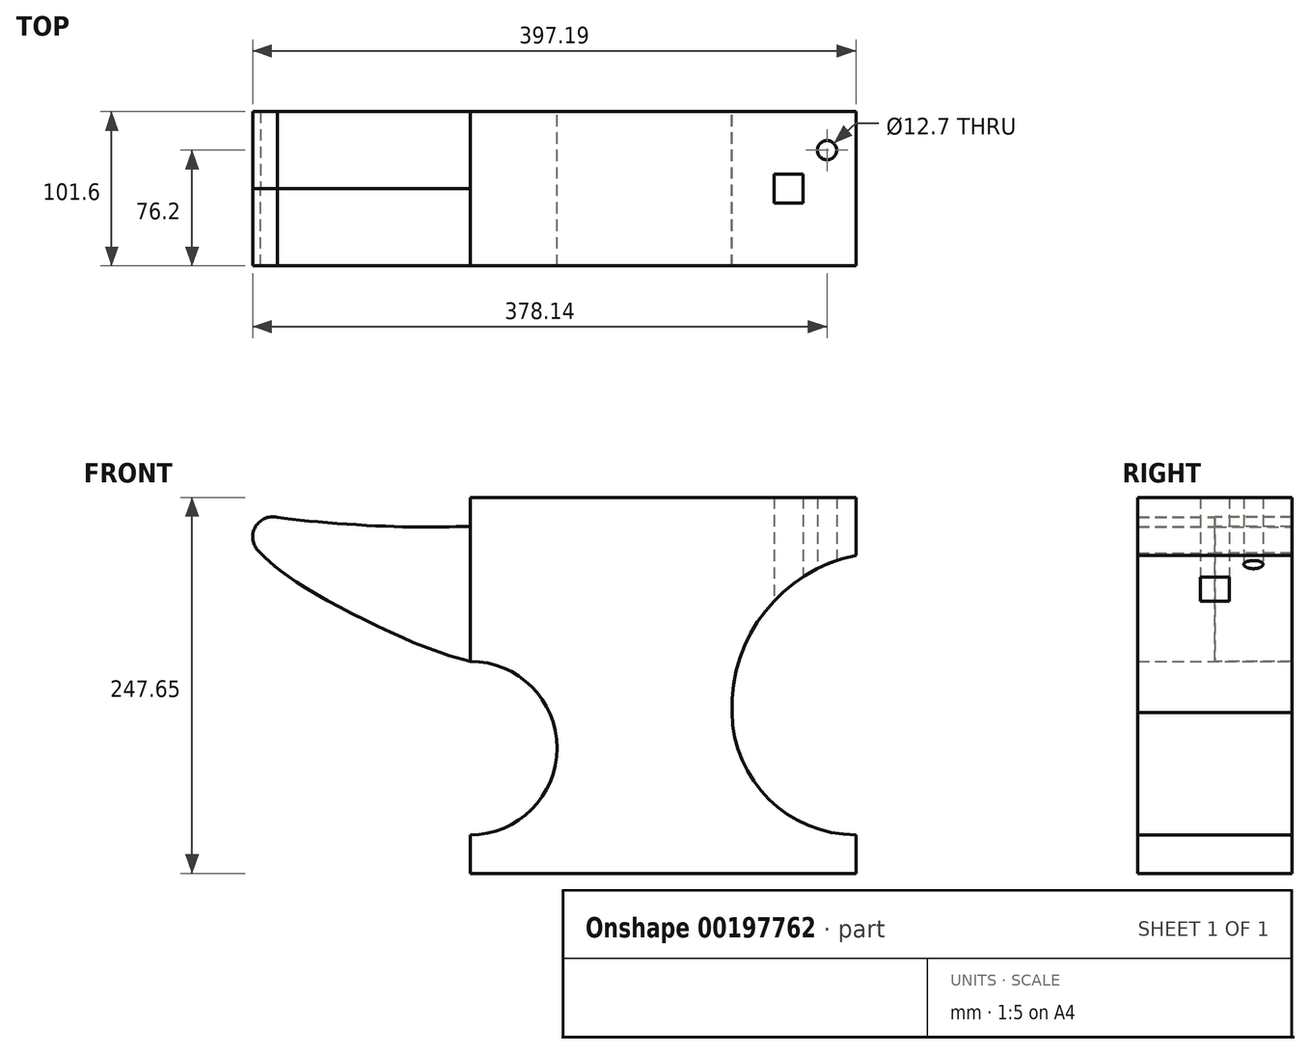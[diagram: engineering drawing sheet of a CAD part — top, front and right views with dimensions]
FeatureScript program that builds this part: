
annotation { "Feature Type Name" : "Feature", "Feature Type Description" : "" }
export const myFeature = defineFeature(function(context is Context, id is Id, definition is map)
    precondition{}
    {
        {
            var Q0;
            Q0=qCreatedBy(makeId("Front.planeOp"),FACE);
            var sketch = newSketch(context, id + "F0", { "sketchPlane" : qUnion([Q0])});
            skLineSegment(sketch, "E0.top", {"start": v(127, 101.6) * mm, "end": v(-127, 101.6) * mm});
            skLineSegment(sketch, "E0.left", {"start": v(127, 82.55) * mm, "end": v(127, 101.6) * mm});
            skLineSegment(sketch, "E0.right", {"start": v(-127, 12.7) * mm, "end": v(-127, 101.6) * mm});
            skPoint(sketch, "E0.middle", {"position": v(0, 0) * mm});
            skPoint(sketch, "E1", {"position": v(88.9, -101.6) * mm});
            skPoint(sketch, "E2", {"position": v(-101.6, -101.6) * mm});
            skPoint(sketch, "E3", {"position": v(127, 82.55) * mm});
            skArc(sketch, "E4", {"start": v(127, 82.55) * mm, "mid": v(62.88, 39.66) * mm, "end": v(46.89, -35.8) * mm});
            skPoint(sketch, "E5", {"position": v(-127, 12.7) * mm});
            skPoint(sketch, "E6.orphan", {"position": v(-127, -101.6) * mm});
            skPoint(sketch, "E7.orphan", {"position": v(127, -101.6) * mm});
            skLineSegment(sketch, "E8", {"start": v(-101.6, -127) * mm, "end": v(88.9, -127) * mm});
            skArc(sketch, "E9", {"start": v(-127, -101.6) * mm, "mid": v(-69.85, -44.45) * mm, "end": v(-127, 12.7) * mm});
            skLineSegment(sketch, "E10", {"start": v(-127, -101.6) * mm, "end": v(-127, -127) * mm});
            skLineSegment(sketch, "E11", {"start": v(-127, -127) * mm, "end": v(-101.6, -127) * mm});
            skFitSpline(sketch, "E12", {"points": [v(-127, 101.6) * mm, v(-180.15, 101.6) * mm, v(-254, 107.6) * mm], "startDerivative": vector(-105.69, -3.09) * mm, "endDerivative": vector(-99.9, 15.17) * mm});
            skArc(sketch, "E13", {"start": v(-254, 107.6) * mm, "mid": v(-268.91, 100.3) * mm, "end": v(-265.09, 84.16) * mm});
            skFitSpline(sketch, "E14", {"points": [v(-265.09, 84.16) * mm, v(-241.14, 64.74) * mm, v(-161.2, 23.88) * mm, v(-127, 12.7) * mm], "startDerivative": vector(69.32, -66.83) * mm, "endDerivative": vector(101.66, -27) * mm});
            skLineSegment(sketch, "E15", {"start": v(-127, 101.6) * mm, "end": v(-127, 120.65) * mm});
            skLineSegment(sketch, "E16", {"start": v(-127, 120.65) * mm, "end": v(127, 120.65) * mm});
            skLineSegment(sketch, "E17", {"start": v(127, 120.65) * mm, "end": v(127, 101.6) * mm});
            skLineSegment(sketch, "E18", {"start": v(127, -101.6) * mm, "end": v(127, -127) * mm});
            skLineSegment(sketch, "E19", {"start": v(127, -127) * mm, "end": v(88.9, -127) * mm});
            skArc(sketch, "E20", {"start": v(45.34, -21.1) * mm, "mid": v(69.67, -78.1) * mm, "end": v(127, -101.6) * mm});
            skSolve(sketch);
        }
        {
            var Q0;
            Q0=makeQuery(id+"F0.imprint","IMPRINT",FACE,{"disambiguationData":[TD([[makeQuery(id+"F0.imprint","IMPRINT",EDGE,{"derivedFrom":sQuery(id+"F0.wireOp",EDGE,"E0.bottom")}),-1.0]])]});
            var Q1;
            Q1=makeQuery(id+"F0.imprint","IMPRINT",FACE,{"disambiguationData":[TD([[makeQuery(id+"F0.imprint","IMPRINT",EDGE,{"derivedFrom":sQuery(id+"F0.wireOp",EDGE,"E0.top")}),-1.0]])]});
            extrude(context, id + "F1", {"entities" : qUnion([Q0, Q1]), "depth" : 50.8 * mm});
        }
        {
            var Q0;
            Q0=makeQuery(id+"F0.imprint","IMPRINT",FACE,{"disambiguationData":[TD([[makeQuery(id+"F0.imprint","IMPRINT",EDGE,{"derivedFrom":sQuery(id+"F0.wireOp",EDGE,"E0.bottom")}),1.0]])]});
            var Q1;
            Q1=makeQuery(id+"F0.imprint","IMPRINT",FACE,{"disambiguationData":[TD([[makeQuery(id+"F0.imprint","IMPRINT",EDGE,{"derivedFrom":sQuery(id+"F0.wireOp",EDGE,"E0.top")}),1.0]])]});
            var Q2;
            Q2=makeQuery(id+"F1.opExtrude","CAP_FACE",FACE,{"disambiguationData":[OSD([sQuery(id+"F0.wireOp",EDGE,"E0.bottom"),sQuery(id+"F0.wireOp",EDGE,"E0.top"),sQuery(id+"F0.wireOp",EDGE,"E0.left"),sQuery(id+"F0.wireOp",EDGE,"E0.right"),sQuery(id+"F0.wireOp",EDGE,"E4"),sQuery(id+"F0.wireOp",EDGE,"5aee445f-a930-434b-87f0-12a5ad99f01d"),sQuery(id+"F0.wireOp",EDGE,"E9")])],"isStart":false});
            extrude(context, id + "F2", {"entities" : qUnion([Q0, Q1]), "operationType" : NewBodyOperationType.ADD, "endBound" : BoundingType.UP_TO_SURFACE, "endBoundEntityFace" : qUnion([Q2]), "depth" : 25.4 * mm});
        }
        {
            var Q0;
            Q0=makeQuery(id+"F1.opExtrude","SWEPT_BODY",BODY,{"disambiguationData":[OSD([sQuery(id+"F0.wireOp",EDGE,"E0.bottom"),sQuery(id+"F0.wireOp",EDGE,"E0.top"),sQuery(id+"F0.wireOp",EDGE,"E0.left"),sQuery(id+"F0.wireOp",EDGE,"E0.right"),sQuery(id+"F0.wireOp",EDGE,"E4"),sQuery(id+"F0.wireOp",EDGE,"f0c81754-0c6e-45d1-96c7-393c20b10861")])]});
            var Q1;
            Q1=makeQuery(id+"F1.opExtrude","CAP_FACE",FACE,{"disambiguationData":[OSD([sQuery(id+"F0.wireOp",EDGE,"E0.bottom"),sQuery(id+"F0.wireOp",EDGE,"E0.top"),sQuery(id+"F0.wireOp",EDGE,"E0.left"),sQuery(id+"F0.wireOp",EDGE,"E0.right"),sQuery(id+"F0.wireOp",EDGE,"E4"),sQuery(id+"F0.wireOp",EDGE,"f0c81754-0c6e-45d1-96c7-393c20b10861")])],"isStart":true});
            mirror(context, id + "F3", {"operationType" : NewBodyOperationType.ADD, "entities" : qUnion([Q0]), "mirrorPlane" : qUnion([Q1])});
        }
        {
            var Q0;
            Q0=qCreatedBy(makeId("Top.planeOp"),FACE);
            var sketch = newSketch(context, id + "F4", { "sketchPlane" : qUnion([Q0])});
            skPoint(sketch, "E21", {"position": v(82.55, 0) * mm});
            skPoint(sketch, "E22", {"position": v(107.95, 25.4) * mm});
            skCircle(sketch, "E23", {"center": v(107.95, 25.4) * mm, "radius": 6.35 * mm});
            skLineSegment(sketch, "E24.bottom", {"start": v(92.08, -9.53) * mm, "end": v(73.03, -9.53) * mm});
            skLineSegment(sketch, "E24.top", {"start": v(92.08, 9.52) * mm, "end": v(73.03, 9.52) * mm});
            skLineSegment(sketch, "E24.left", {"start": v(92.08, -9.53) * mm, "end": v(92.08, 9.52) * mm});
            skLineSegment(sketch, "E24.right", {"start": v(73.03, -9.53) * mm, "end": v(73.03, 9.52) * mm});
            skSolve(sketch);
        }
        {
            var Q0;
            Q0=makeQuery(id+"F4.imprint","IMPRINT",FACE,{"disambiguationData":[TD([[makeQuery(id+"F4.imprint","IMPRINT",EDGE,{"derivedFrom":sQuery(id+"F4.wireOp",EDGE,"E24.bottom")}),-1.0]])]});
            var Q1;
            Q1=makeQuery(id+"F4.imprint","IMPRINT",FACE,{"disambiguationData":[TD([[makeQuery(id+"F4.imprint","IMPRINT",EDGE,{"derivedFrom":sQuery(id+"F4.wireOp",EDGE,"E23")}),1.0]])]});
            extrude(context, id + "F5", {"entities" : qUnion([Q0, Q1]), "operationType" : NewBodyOperationType.REMOVE, "depth" : 127 * mm});
        }
        {
            var Q0;
            Q0=makeQuery(id+"F0.imprint","IMPRINT",FACE,{"disambiguationData":[TD([[makeQuery(id+"F0.imprint","IMPRINT",EDGE,{"derivedFrom":sQuery(id+"F0.wireOp",EDGE,"E0.right")}),1.0]])]});
            extrude(context, id + "F7", {"entities" : qUnion([Q0]), "depth" : 50.8 * mm});
        }
        {
            var Q0;
            Q0=makeQuery(id+"F7.opExtrude","SWEPT_BODY",BODY,{"disambiguationData":[OSD([sQuery(id+"F0.wireOp",EDGE,"E0.right"),sQuery(id+"F0.wireOp",EDGE,"E12"),sQuery(id+"F0.wireOp",EDGE,"E13"),sQuery(id+"F0.wireOp",EDGE,"E14")])]});
            var Q1;
            Q1=qCreatedBy(makeId("Front.planeOp"),FACE);
            mirror(context, id + "F6", {"entities" : qUnion([Q0]), "mirrorPlane" : qUnion([Q1])});
        }
    });
